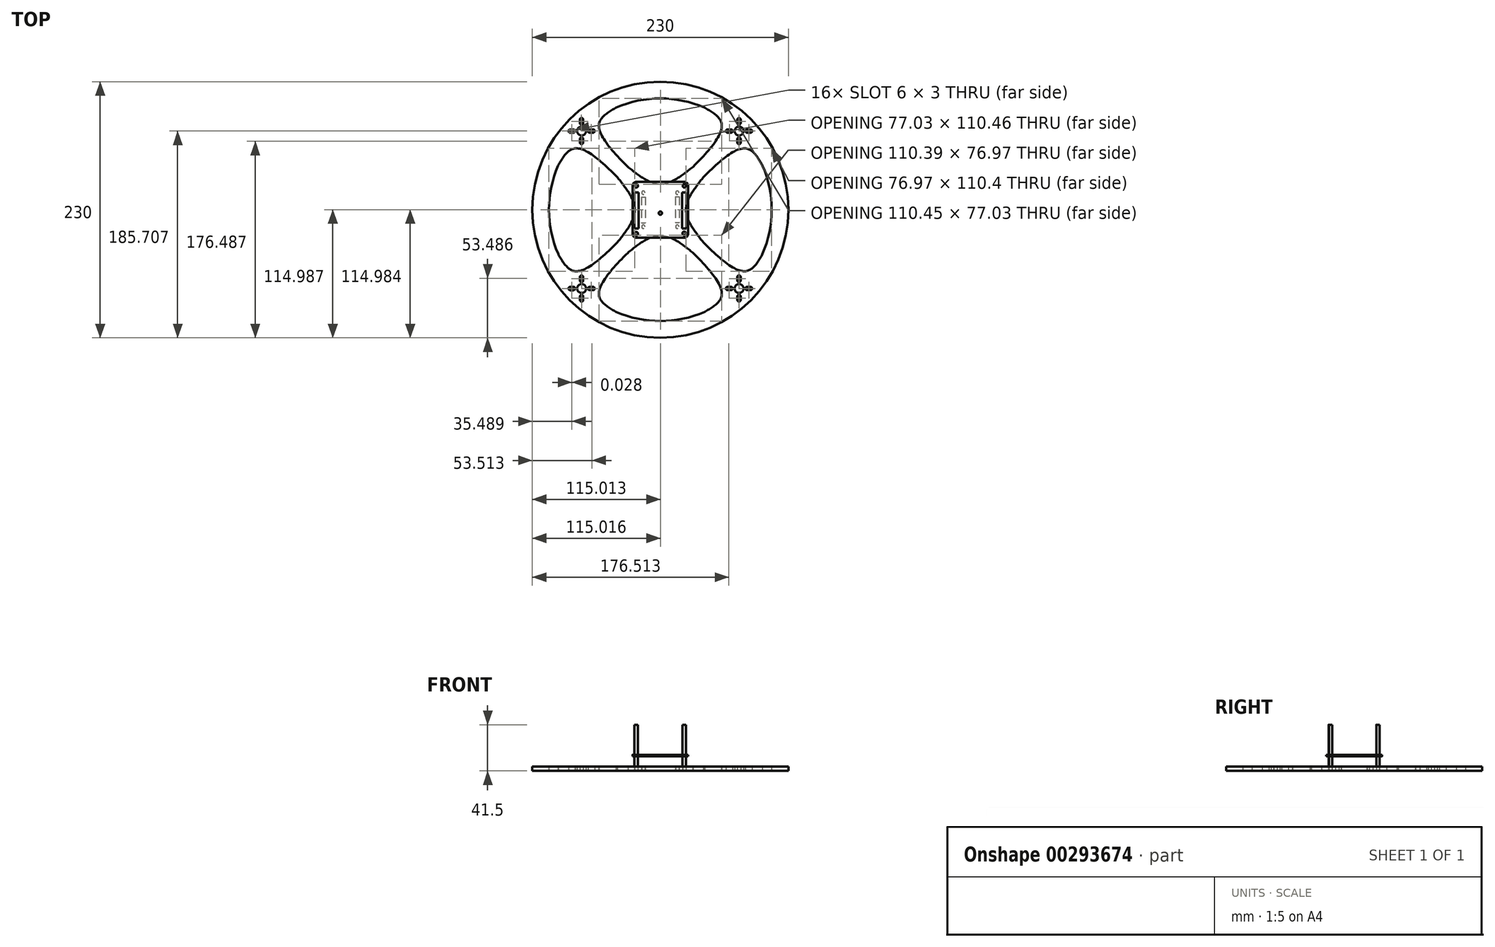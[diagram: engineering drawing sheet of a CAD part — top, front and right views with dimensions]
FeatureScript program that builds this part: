
annotation { "Feature Type Name" : "Feature", "Feature Type Description" : "" }
export const myFeature = defineFeature(function(context is Context, id is Id, definition is map)
    precondition{}
    {
        {
            var Q0;
            Q0=qCreatedBy(makeId("Top.planeOp"),FACE);
            var sketch = newSketch(context, id + "F0", { "sketchPlane" : qUnion([Q0])});
            skCircle(sketch, "E0", {"center": v(0, 0) * mm, "radius": 115 * mm});
            skCircle(sketch, "E1", {"center": v(0, 0) * mm, "radius": 100 * mm});
            skLineSegment(sketch, "E2.bottom", {"start": v(-17.97, 17.97) * mm, "end": v(18.03, 17.97) * mm});
            skLineSegment(sketch, "E2.left", {"start": v(-17.97, 17.97) * mm, "end": v(-17.97, -18.03) * mm});
            skLineSegment(sketch, "E2.right", {"start": v(18.03, 17.97) * mm, "end": v(18.03, -18.03) * mm});
            skLineSegment(sketch, "E3", {"start": v(-17.97, 17.97) * mm, "end": v(18.03, -18.03) * mm});
            skLineSegment(sketch, "E4", {"start": v(18.03, 17.97) * mm, "end": v(-17.97, -18.03) * mm});
            skLineSegment(sketch, "E5.bottom", {"start": v(-15.28, 15.28) * mm, "end": v(15.22, 15.28) * mm});
            skLineSegment(sketch, "E5.top", {"start": v(-15.28, -15.22) * mm, "end": v(15.22, -15.22) * mm});
            skLineSegment(sketch, "E5.left", {"start": v(-15.28, 15.28) * mm, "end": v(-15.28, -15.22) * mm});
            skLineSegment(sketch, "E5.right", {"start": v(15.22, 15.28) * mm, "end": v(15.22, -15.22) * mm});
            skCircle(sketch, "E6", {"center": v(-15.28, -15.22) * mm, "radius": 1.5 * mm});
            skCircle(sketch, "E7", {"center": v(15.22, -15.22) * mm, "radius": 1.5 * mm});
            skCircle(sketch, "E8", {"center": v(15.22, 15.28) * mm, "radius": 1.5 * mm});
            skCircle(sketch, "E9", {"center": v(-15.28, 15.28) * mm, "radius": 1.5 * mm});
            skLineSegment(sketch, "E10", {"start": v(18.03, 17.97) * mm, "end": v(-81.29, -81.35) * mm});
            skLineSegment(sketch, "E11", {"start": v(-81.29, -81.35) * mm, "end": v(81.34, 81.3) * mm});
            skLineSegment(sketch, "E12", {"start": v(-17.97, 17.97) * mm, "end": v(81.32, -81.32) * mm});
            skLineSegment(sketch, "E13", {"start": v(81.32, -81.32) * mm, "end": v(-81.32, 81.32) * mm});
            skPoint(sketch, "E14", {"position": v(-70.68, -70.74) * mm});
            skPoint(sketch, "E15", {"position": v(70.71, -70.71) * mm});
            skPoint(sketch, "E16", {"position": v(76.01, -76.01) * mm});
            skPoint(sketch, "E17", {"position": v(-63.56, -63.68) * mm});
            skPoint(sketch, "E18", {"position": v(-75.98, -76.04) * mm});
            skPoint(sketch, "E19", {"position": v(-65.18, -75.84) * mm});
            skPoint(sketch, "E20", {"position": v(-75.78, -65.24) * mm});
            skLineSegment(sketch, "E21", {"start": v(-65.18, -75.84) * mm, "end": v(-55.18, -75.84) * mm});
            skLineSegment(sketch, "E22", {"start": v(-75.78, -65.24) * mm, "end": v(-75.78, -55.24) * mm});
            skLineSegment(sketch, "E23", {"start": v(-17.97, -18.03) * mm, "end": v(18.03, -18.03) * mm});
            skPoint(sketch, "E24", {"position": v(65.21, -75.81) * mm});
            skPoint(sketch, "E25", {"position": v(75.81, -65.21) * mm});
            skPoint(sketch, "E26", {"position": v(65.24, 75.79) * mm});
            skPoint(sketch, "E27", {"position": v(75.83, 65.19) * mm});
            skPoint(sketch, "E28", {"position": v(-65.21, 75.81) * mm});
            skPoint(sketch, "E29", {"position": v(-75.81, 65.21) * mm});
            skPoint(sketch, "E30", {"position": v(70.73, 70.69) * mm});
            skPoint(sketch, "E31", {"position": v(-70.71, 70.71) * mm});
            skLineSegment(sketch, "E32", {"start": v(65.21, -75.81) * mm, "end": v(55.21, -75.81) * mm});
            skLineSegment(sketch, "E33", {"start": v(75.81, -65.21) * mm, "end": v(75.81, -55.21) * mm});
            skPoint(sketch, "E34", {"position": v(39.8, -91.74) * mm});
            skPoint(sketch, "E35", {"position": v(91.74, -39.8) * mm});
            skPoint(sketch, "E36", {"position": v(-39.75, -91.76) * mm});
            skPoint(sketch, "E37", {"position": v(-91.73, -39.83) * mm});
            skLineSegment(sketch, "E38", {"start": v(75.83, 65.19) * mm, "end": v(75.83, 55.19) * mm});
            skLineSegment(sketch, "E39", {"start": v(65.24, 75.79) * mm, "end": v(55.24, 75.79) * mm});
            skLineSegment(sketch, "E40", {"start": v(-65.21, 75.81) * mm, "end": v(-55.21, 75.81) * mm});
            skLineSegment(sketch, "E41", {"start": v(-75.81, 65.21) * mm, "end": v(-75.81, 55.21) * mm});
            skPoint(sketch, "E42", {"position": v(91.76, 39.76) * mm});
            skPoint(sketch, "E43", {"position": v(39.82, 91.73) * mm});
            skPoint(sketch, "E44", {"position": v(-39.8, 91.74) * mm});
            skPoint(sketch, "E45", {"position": v(-91.74, 39.8) * mm});
            skFitSpline(sketch, "E46", {"points": [v(-7.37, -18.03) * mm, v(-55.18, -75.84) * mm, v(-39.75, -91.76) * mm], "startDerivative": vector(-111.89, -103.5) * mm, "endDerivative": vector(64.51, -37.45) * mm});
            skFitSpline(sketch, "E47", {"points": [v(-17.97, -7.43) * mm, v(-75.78, -55.24) * mm, v(-91.73, -39.83) * mm], "startDerivative": vector(-103.48, -111.9) * mm, "endDerivative": vector(-37.52, 64.47) * mm});
            skFitSpline(sketch, "E48", {"points": [v(-17.97, 7.37) * mm, v(-75.81, 55.21) * mm, v(-91.74, 39.8) * mm], "startDerivative": vector(-103.54, 111.94) * mm, "endDerivative": vector(-37.49, -64.5) * mm});
            skFitSpline(sketch, "E49", {"points": [v(-7.37, 17.97) * mm, v(-55.21, 75.81) * mm, v(-39.8, 91.74) * mm], "startDerivative": vector(-111.94, 103.54) * mm, "endDerivative": vector(64.5, 37.49) * mm});
            skFitSpline(sketch, "E50", {"points": [v(7.43, 17.97) * mm, v(55.24, 75.79) * mm, v(39.82, 91.73) * mm], "startDerivative": vector(111.89, 103.5) * mm, "endDerivative": vector(-64.47, 37.51) * mm});
            skFitSpline(sketch, "E51", {"points": [v(18.03, 7.37) * mm, v(75.83, 55.19) * mm, v(91.76, 39.76) * mm], "startDerivative": vector(103.5, 111.9) * mm, "endDerivative": vector(37.46, -64.51) * mm});
            skFitSpline(sketch, "E52", {"points": [v(18.03, -7.43) * mm, v(75.81, -55.21) * mm, v(91.74, -39.8) * mm], "startDerivative": vector(103.45, -111.84) * mm, "endDerivative": vector(37.48, 64.48) * mm});
            skFitSpline(sketch, "E53", {"points": [v(7.43, -18.03) * mm, v(55.21, -75.81) * mm, v(39.8, -91.74) * mm], "startDerivative": vector(111.84, -103.45) * mm, "endDerivative": vector(-64.48, -37.48) * mm});
            skPoint(sketch, "E54", {"position": v(38.62, 29.2) * mm});
            skPoint(sketch, "E55", {"position": v(38.62, -29.24) * mm});
            skPoint(sketch, "E56", {"position": v(-38.56, -29.25) * mm});
            skPoint(sketch, "E57", {"position": v(-29.2, -38.62) * mm});
            skPoint(sketch, "E58", {"position": v(-38.56, 29.2) * mm});
            skPoint(sketch, "E59", {"position": v(-29.2, 38.56) * mm});
            skPoint(sketch, "E60", {"position": v(29.24, 38.57) * mm});
            skPoint(sketch, "E61", {"position": v(29.03, -38.4) * mm});
            skPoint(sketch, "E62", {"position": v(-22.97, -0.03) * mm});
            skPoint(sketch, "E62.positionSnap0", {"position": v(-17.97, -0.03) * mm});
            skFitSpline(sketch, "E63", {"points": [v(-38.56, 29.2) * mm, v(-22.97, -0.03) * mm, v(-38.56, -29.25) * mm], "startDerivative": vector(46.77, -58.44) * mm, "endDerivative": vector(-46.77, -58.44) * mm});
            skPoint(sketch, "E64", {"position": v(0, -23.03) * mm});
            skPoint(sketch, "E65", {"position": v(23.03, 0) * mm});
            skPoint(sketch, "E66", {"position": v(0, 22.97) * mm});
            skPoint(sketch, "E67", {"position": v(0, 17.97) * mm});
            skPoint(sketch, "E68", {"position": v(0, -18.03) * mm});
            skFitSpline(sketch, "E69", {"points": [v(-29.2, -38.62) * mm, v(0, -23.03) * mm, v(29.03, -38.4) * mm], "startDerivative": vector(58.3, 46.64) * mm, "endDerivative": vector(58.13, -46.26) * mm});
            skFitSpline(sketch, "E70", {"points": [v(38.62, -29.24) * mm, v(23.03, 0) * mm, v(38.62, 29.2) * mm], "startDerivative": vector(-46.77, 58.48) * mm, "endDerivative": vector(46.78, 58.4) * mm});
            skFitSpline(sketch, "E71", {"points": [v(-29.2, 38.56) * mm, v(0, 22.97) * mm, v(29.24, 38.57) * mm], "startDerivative": vector(58.4, -46.78) * mm, "endDerivative": vector(58.48, 46.77) * mm});
            skPoint(sketch, "E72", {"position": v(-70.7, 70.7) * mm});
            skCircle(sketch, "E73", {"center": v(-70.7, 70.7) * mm, "radius": 4 * mm});
            skLineSegment(sketch, "E74.left", {"start": v(-69.26, 63.46) * mm, "end": v(-69.26, 60.46) * mm});
            skLineSegment(sketch, "E75", {"start": v(-72.26, 63.46) * mm, "end": v(-72.26, 60.46) * mm});
            skArc(sketch, "E76", {"start": v(-69.26, 63.46) * mm, "mid": v(-70.76, 64.96) * mm, "end": v(-72.26, 63.46) * mm});
            skArc(sketch, "E77", {"start": v(-72.26, 60.46) * mm, "mid": v(-70.76, 58.96) * mm, "end": v(-69.26, 60.46) * mm});
            skLineSegment(sketch, "E78.left", {"start": v(-60.51, 69.21) * mm, "end": v(-63.51, 69.21) * mm});
            skLineSegment(sketch, "E79", {"start": v(-60.51, 72.21) * mm, "end": v(-63.51, 72.21) * mm});
            skArc(sketch, "E80", {"start": v(-60.51, 69.21) * mm, "mid": v(-59.01, 70.71) * mm, "end": v(-60.51, 72.21) * mm});
            skArc(sketch, "E81", {"start": v(-63.51, 72.21) * mm, "mid": v(-65.01, 70.71) * mm, "end": v(-63.51, 69.21) * mm});
            skLineSegment(sketch, "E82.left", {"start": v(-81.01, 72.2) * mm, "end": v(-78.01, 72.2) * mm});
            skLineSegment(sketch, "E83", {"start": v(-81.01, 69.2) * mm, "end": v(-78.01, 69.2) * mm});
            skArc(sketch, "E84", {"start": v(-81.01, 72.2) * mm, "mid": v(-82.51, 70.7) * mm, "end": v(-81.01, 69.2) * mm});
            skArc(sketch, "E85", {"start": v(-78.01, 69.2) * mm, "mid": v(-76.51, 70.7) * mm, "end": v(-78.01, 72.2) * mm});
            skLineSegment(sketch, "E86.left", {"start": v(-69.3, 80.96) * mm, "end": v(-69.3, 77.96) * mm});
            skLineSegment(sketch, "E87", {"start": v(-72.3, 80.96) * mm, "end": v(-72.3, 77.96) * mm});
            skArc(sketch, "E88", {"start": v(-69.3, 80.96) * mm, "mid": v(-70.8, 82.46) * mm, "end": v(-72.3, 80.96) * mm});
            skArc(sketch, "E89", {"start": v(-72.3, 77.96) * mm, "mid": v(-70.8, 76.46) * mm, "end": v(-69.3, 77.96) * mm});
            skCircle(sketch, "E90", {"center": v(-70.68, -70.74) * mm, "radius": 4 * mm});
            skLineSegment(sketch, "E91.left", {"start": v(-69.23, -78) * mm, "end": v(-69.23, -81) * mm});
            skLineSegment(sketch, "E92", {"start": v(-72.23, -78) * mm, "end": v(-72.23, -81) * mm});
            skArc(sketch, "E93", {"start": v(-69.23, -78) * mm, "mid": v(-70.73, -76.5) * mm, "end": v(-72.23, -78) * mm});
            skArc(sketch, "E94", {"start": v(-72.23, -81) * mm, "mid": v(-70.73, -82.5) * mm, "end": v(-69.23, -81) * mm});
            skLineSegment(sketch, "E95.left", {"start": v(-60.48, -72.24) * mm, "end": v(-63.48, -72.24) * mm});
            skLineSegment(sketch, "E96", {"start": v(-60.48, -69.24) * mm, "end": v(-63.48, -69.24) * mm});
            skArc(sketch, "E97", {"start": v(-60.48, -72.24) * mm, "mid": v(-58.98, -70.74) * mm, "end": v(-60.48, -69.24) * mm});
            skArc(sketch, "E98", {"start": v(-63.48, -69.24) * mm, "mid": v(-64.98, -70.74) * mm, "end": v(-63.48, -72.24) * mm});
            skLineSegment(sketch, "E99.left", {"start": v(-80.98, -69.24) * mm, "end": v(-77.98, -69.24) * mm});
            skLineSegment(sketch, "E100", {"start": v(-80.98, -72.24) * mm, "end": v(-77.98, -72.24) * mm});
            skArc(sketch, "E101", {"start": v(-80.98, -69.24) * mm, "mid": v(-82.48, -70.74) * mm, "end": v(-80.98, -72.24) * mm});
            skArc(sketch, "E102", {"start": v(-77.98, -72.24) * mm, "mid": v(-76.48, -70.74) * mm, "end": v(-77.98, -69.24) * mm});
            skLineSegment(sketch, "E103.left", {"start": v(-69.27, -60.5) * mm, "end": v(-69.27, -63.5) * mm});
            skLineSegment(sketch, "E104", {"start": v(-72.27, -60.5) * mm, "end": v(-72.27, -63.5) * mm});
            skArc(sketch, "E105", {"start": v(-69.27, -60.5) * mm, "mid": v(-70.77, -59) * mm, "end": v(-72.27, -60.5) * mm});
            skArc(sketch, "E106", {"start": v(-72.27, -63.5) * mm, "mid": v(-70.77, -65) * mm, "end": v(-69.27, -63.5) * mm});
            skCircle(sketch, "E107", {"center": v(70.71, -70.71) * mm, "radius": 4 * mm});
            skLineSegment(sketch, "E108.left", {"start": v(72.16, -77.96) * mm, "end": v(72.16, -80.96) * mm});
            skLineSegment(sketch, "E109", {"start": v(69.16, -77.96) * mm, "end": v(69.16, -80.96) * mm});
            skArc(sketch, "E110", {"start": v(72.16, -77.96) * mm, "mid": v(70.66, -76.46) * mm, "end": v(69.16, -77.96) * mm});
            skArc(sketch, "E111", {"start": v(69.16, -80.96) * mm, "mid": v(70.66, -82.46) * mm, "end": v(72.16, -80.96) * mm});
            skLineSegment(sketch, "E112.left", {"start": v(80.9, -72.2) * mm, "end": v(77.9, -72.2) * mm});
            skLineSegment(sketch, "E113", {"start": v(80.9, -69.2) * mm, "end": v(77.9, -69.2) * mm});
            skArc(sketch, "E114", {"start": v(80.9, -72.2) * mm, "mid": v(82.4, -70.7) * mm, "end": v(80.9, -69.2) * mm});
            skArc(sketch, "E115", {"start": v(77.9, -69.2) * mm, "mid": v(76.4, -70.7) * mm, "end": v(77.9, -72.2) * mm});
            skLineSegment(sketch, "E116.left", {"start": v(60.4, -69.21) * mm, "end": v(63.4, -69.21) * mm});
            skLineSegment(sketch, "E117", {"start": v(60.4, -72.21) * mm, "end": v(63.4, -72.21) * mm});
            skArc(sketch, "E118", {"start": v(60.4, -69.21) * mm, "mid": v(58.9, -70.71) * mm, "end": v(60.4, -72.21) * mm});
            skArc(sketch, "E119", {"start": v(63.4, -72.21) * mm, "mid": v(64.9, -70.71) * mm, "end": v(63.4, -69.21) * mm});
            skLineSegment(sketch, "E120.left", {"start": v(72.13, -60.46) * mm, "end": v(72.13, -63.46) * mm});
            skLineSegment(sketch, "E121", {"start": v(69.13, -60.46) * mm, "end": v(69.13, -63.46) * mm});
            skArc(sketch, "E122", {"start": v(72.13, -60.46) * mm, "mid": v(70.63, -58.96) * mm, "end": v(69.13, -60.46) * mm});
            skArc(sketch, "E123", {"start": v(69.13, -63.46) * mm, "mid": v(70.63, -64.96) * mm, "end": v(72.13, -63.46) * mm});
            skCircle(sketch, "E124", {"center": v(70.73, 70.69) * mm, "radius": 4 * mm});
            skLineSegment(sketch, "E125.left", {"start": v(72.18, 63.44) * mm, "end": v(72.18, 60.44) * mm});
            skLineSegment(sketch, "E126", {"start": v(69.18, 63.44) * mm, "end": v(69.18, 60.44) * mm});
            skArc(sketch, "E127", {"start": v(72.18, 63.44) * mm, "mid": v(70.68, 64.94) * mm, "end": v(69.18, 63.44) * mm});
            skArc(sketch, "E128", {"start": v(69.18, 60.44) * mm, "mid": v(70.68, 58.94) * mm, "end": v(72.18, 60.44) * mm});
            skLineSegment(sketch, "E129.left", {"start": v(80.93, 69.19) * mm, "end": v(77.93, 69.19) * mm});
            skLineSegment(sketch, "E130", {"start": v(80.93, 72.19) * mm, "end": v(77.93, 72.19) * mm});
            skArc(sketch, "E131", {"start": v(80.93, 69.19) * mm, "mid": v(82.43, 70.69) * mm, "end": v(80.93, 72.19) * mm});
            skArc(sketch, "E132", {"start": v(77.93, 72.19) * mm, "mid": v(76.43, 70.69) * mm, "end": v(77.93, 69.19) * mm});
            skLineSegment(sketch, "E133.left", {"start": v(60.43, 72.18) * mm, "end": v(63.43, 72.18) * mm});
            skLineSegment(sketch, "E134", {"start": v(60.43, 69.18) * mm, "end": v(63.43, 69.18) * mm});
            skArc(sketch, "E135", {"start": v(60.43, 72.18) * mm, "mid": v(58.93, 70.68) * mm, "end": v(60.43, 69.18) * mm});
            skArc(sketch, "E136", {"start": v(63.43, 69.18) * mm, "mid": v(64.93, 70.68) * mm, "end": v(63.43, 72.18) * mm});
            skLineSegment(sketch, "E137.left", {"start": v(72.15, 80.94) * mm, "end": v(72.15, 77.94) * mm});
            skLineSegment(sketch, "E138", {"start": v(69.15, 80.94) * mm, "end": v(69.15, 77.94) * mm});
            skArc(sketch, "E139", {"start": v(72.15, 80.94) * mm, "mid": v(70.65, 82.44) * mm, "end": v(69.15, 80.94) * mm});
            skArc(sketch, "E140", {"start": v(69.15, 77.94) * mm, "mid": v(70.65, 76.44) * mm, "end": v(72.15, 77.94) * mm});
            skPoint(sketch, "E141", {"position": v(-21.5, -21.56) * mm});
            skCircle(sketch, "E142", {"center": v(-21.5, -21.56) * mm, "radius": 1.5 * mm});
            skPoint(sketch, "E143", {"position": v(21.56, -21.56) * mm});
            skPoint(sketch, "E144", {"position": v(21.56, 21.5) * mm});
            skPoint(sketch, "E145", {"position": v(-21.5, 21.5) * mm});
            skCircle(sketch, "E146", {"center": v(-21.5, 21.5) * mm, "radius": 1.5 * mm});
            skCircle(sketch, "E147", {"center": v(21.56, 21.5) * mm, "radius": 1.5 * mm});
            skCircle(sketch, "E148", {"center": v(21.56, -21.56) * mm, "radius": 1.5 * mm});
            skLineSegment(sketch, "E149.left", {"start": v(-15.24, 11.66) * mm, "end": v(-15.24, -11.59) * mm});
            skLineSegment(sketch, "E150.left", {"start": v(15.22, 11.64) * mm, "end": v(15.22, -11.61) * mm});
            skLineSegment(sketch, "E151.bottom", {"start": v(-17.03, 11.57) * mm, "end": v(-13.53, 11.57) * mm});
            skLineSegment(sketch, "E151.top", {"start": v(-17.03, -11.68) * mm, "end": v(-13.53, -11.68) * mm});
            skLineSegment(sketch, "E151.left", {"start": v(-17.03, 11.57) * mm, "end": v(-17.03, -11.68) * mm});
            skLineSegment(sketch, "E151.right", {"start": v(-13.53, 11.57) * mm, "end": v(-13.53, -11.68) * mm});
            skLineSegment(sketch, "E152.bottom", {"start": v(13.37, 11.76) * mm, "end": v(16.87, 11.76) * mm});
            skLineSegment(sketch, "E152.top", {"start": v(13.37, -11.5) * mm, "end": v(16.87, -11.5) * mm});
            skLineSegment(sketch, "E152.left", {"start": v(13.37, 11.76) * mm, "end": v(13.37, -11.5) * mm});
            skLineSegment(sketch, "E152.right", {"start": v(16.87, 11.76) * mm, "end": v(16.87, -11.5) * mm});
            skSolve(sketch);
        }
        {
            var Q0;
            Q0=qCreatedBy(makeId("Top.planeOp"),FACE);
            var sketch = newSketch(context, id + "F1", { "sketchPlane" : qUnion([Q0])});
            skLineSegment(sketch, "E153.bottom", {"start": v(21.53, 21.51) * mm, "end": v(-21.54, 21.51) * mm});
            skLineSegment(sketch, "E153.top", {"start": v(21.53, -21.56) * mm, "end": v(-21.54, -21.56) * mm});
            skLineSegment(sketch, "E153.left", {"start": v(21.53, 21.51) * mm, "end": v(21.53, -21.56) * mm});
            skLineSegment(sketch, "E153.right", {"start": v(-21.54, 21.51) * mm, "end": v(-21.54, -21.56) * mm});
            skPoint(sketch, "E153.middle", {"position": v(0, -0.02) * mm});
            skCircle(sketch, "E154", {"center": v(-21.54, -21.56) * mm, "radius": 1.5 * mm});
            skCircle(sketch, "E155", {"center": v(21.53, -21.56) * mm, "radius": 1.5 * mm});
            skCircle(sketch, "E156", {"center": v(21.53, 21.51) * mm, "radius": 1.5 * mm});
            skCircle(sketch, "E157", {"center": v(-21.54, 21.51) * mm, "radius": 1.5 * mm});
            skLineSegment(sketch, "E158.bottom", {"start": v(-25, 24.98) * mm, "end": v(25, 24.98) * mm});
            skLineSegment(sketch, "E158.top", {"start": v(-25, -25.02) * mm, "end": v(25, -25.02) * mm});
            skLineSegment(sketch, "E158.left", {"start": v(-25, 24.98) * mm, "end": v(-25, -25.02) * mm});
            skLineSegment(sketch, "E158.right", {"start": v(25, 24.98) * mm, "end": v(25, -25.02) * mm});
            skArc(sketch, "E159", {"start": v(21.53, -25.02) * mm, "mid": v(23.98, -24) * mm, "end": v(25, -21.56) * mm});
            skArc(sketch, "E160", {"start": v(-21.54, -25.02) * mm, "mid": v(-24, -24) * mm, "end": v(-25, -21.56) * mm});
            skArc(sketch, "E161", {"start": v(-25, 21.51) * mm, "mid": v(-24, 23.96) * mm, "end": v(-21.54, 24.98) * mm});
            skArc(sketch, "E162", {"start": v(25, 21.51) * mm, "mid": v(23.98, 23.96) * mm, "end": v(21.53, 24.98) * mm});
            skPoint(sketch, "E163", {"position": v(0, -3.02) * mm});
            skCircle(sketch, "E164", {"center": v(0, -3.02) * mm, "radius": 1.5 * mm});
            skLineSegment(sketch, "E165.bottom", {"start": v(-23.36, 15.7) * mm, "end": v(-19.58, 15.7) * mm});
            skLineSegment(sketch, "E165.top", {"start": v(-23.36, -16.77) * mm, "end": v(-19.58, -16.77) * mm});
            skLineSegment(sketch, "E165.left", {"start": v(-23.36, 15.7) * mm, "end": v(-23.36, -16.77) * mm});
            skLineSegment(sketch, "E165.right", {"start": v(-19.58, 15.7) * mm, "end": v(-19.58, -16.77) * mm});
            skLineSegment(sketch, "E166.bottom", {"start": v(19.67, 15.7) * mm, "end": v(23.45, 15.7) * mm});
            skLineSegment(sketch, "E166.top", {"start": v(19.67, -16.77) * mm, "end": v(23.45, -16.77) * mm});
            skLineSegment(sketch, "E166.left", {"start": v(19.67, 15.7) * mm, "end": v(19.67, -16.77) * mm});
            skLineSegment(sketch, "E166.right", {"start": v(23.45, 15.7) * mm, "end": v(23.45, -16.77) * mm});
            skSolve(sketch);
        }
        {
            var Q0;
            {var subQ8=sQuery(id+"F1.wireOp",EDGE,"E159");Q0=makeQuery(id+"F1.imprint","IMPRINT",FACE,{"disambiguationData":[TD([[makeQuery(id+"F1.imprint","IMPRINT",EDGE,{"derivedFrom":subQ8}),1.0]])]});}
            var Q1;
            Q1=makeQuery(id+"F1.imprint","IMPRINT",FACE,{"disambiguationData":[TD([[makeQuery(id+"F1.imprint","IMPRINT",EDGE,{"derivedFrom":sQuery(id+"F1.wireOp",EDGE,"E164")}),-1.0]])]});
            extrude(context, id + "F2", {"entities" : qUnion([Q0, Q1]), "depth" : 1.5 * mm});
        }
        {
            var Q0;
            Q0=makeQuery(id+"F2.opExtrude","SWEPT_BODY",BODY,{"disambiguationData":[OSD([sQuery(id+"F1.wireOp",EDGE,"E154"),sQuery(id+"F1.wireOp",EDGE,"E155"),sQuery(id+"F1.wireOp",EDGE,"E156"),sQuery(id+"F1.wireOp",EDGE,"E157"),sQuery(id+"F1.wireOp",EDGE,"E158.bottom"),sQuery(id+"F1.wireOp",EDGE,"E158.top"),sQuery(id+"F1.wireOp",EDGE,"E158.left"),sQuery(id+"F1.wireOp",EDGE,"E158.right"),sQuery(id+"F1.wireOp",EDGE,"E159"),sQuery(id+"F1.wireOp",EDGE,"E160"),sQuery(id+"F1.wireOp",EDGE,"E161"),sQuery(id+"F1.wireOp",EDGE,"E162"),sQuery(id+"F1.wireOp",EDGE,"E164"),sQuery(id+"F1.wireOp",EDGE,"E165.bottom"),sQuery(id+"F1.wireOp",EDGE,"E165.top"),sQuery(id+"F1.wireOp",EDGE,"E165.left"),sQuery(id+"F1.wireOp",EDGE,"E165.right"),sQuery(id+"F1.wireOp",EDGE,"E166.bottom"),sQuery(id+"F1.wireOp",EDGE,"E166.top"),sQuery(id+"F1.wireOp",EDGE,"E166.left"),sQuery(id+"F1.wireOp",EDGE,"E166.right")])]});
            transform(context, id + "F3", {"entities" : qUnion([Q0]), "transformType" : TransformType.TRANSLATION_3D, "dx" : 0 * mm, "dy" : 0 * mm, "dz" : 13 * mm, "makeCopy" : false});
        }
        {
            var Q0;
            Q0=qCreatedBy(makeId("Top.planeOp"),FACE);
            var sketch = newSketch(context, id + "F4", { "sketchPlane" : qUnion([Q0])});
            skCircle(sketch, "E167", {"center": v(-21.74, 21.47) * mm, "radius": 1.5 * mm});
            skCircle(sketch, "E168", {"center": v(21.56, 21.47) * mm, "radius": 1.5 * mm});
            skCircle(sketch, "E169", {"center": v(21.42, -21.1) * mm, "radius": 1.5 * mm});
            skCircle(sketch, "E170", {"center": v(-21.74, -21.4) * mm, "radius": 1.5 * mm});
            skSolve(sketch);
        }
        {
            var Q0;
            Q0=makeQuery(id+"F4.imprint","IMPRINT",FACE,{"disambiguationData":[TD([[makeQuery(id+"F4.imprint","IMPRINT",EDGE,{"derivedFrom":sQuery(id+"F4.wireOp",EDGE,"E167")}),1.0]])]});
            var Q1;
            Q1=makeQuery(id+"F4.imprint","IMPRINT",FACE,{"disambiguationData":[TD([[makeQuery(id+"F4.imprint","IMPRINT",EDGE,{"derivedFrom":sQuery(id+"F4.wireOp",EDGE,"E170")}),1.0]])]});
            var Q2;
            Q2=makeQuery(id+"F4.imprint","IMPRINT",FACE,{"disambiguationData":[TD([[makeQuery(id+"F4.imprint","IMPRINT",EDGE,{"derivedFrom":sQuery(id+"F4.wireOp",EDGE,"E169")}),1.0]])]});
            var Q3;
            Q3=makeQuery(id+"F4.imprint","IMPRINT",FACE,{"disambiguationData":[TD([[makeQuery(id+"F4.imprint","IMPRINT",EDGE,{"derivedFrom":sQuery(id+"F4.wireOp",EDGE,"E168")}),1.0]])]});
            extrude(context, id + "F5", {"entities" : qUnion([Q0, Q1, Q2, Q3]), "depth" : 41.5 * mm});
        }
        {
            var Q0;
            Q0=makeQuery(id+"F0.imprint","IMPRINT",FACE,{"disambiguationData":[TD([[makeQuery(id+"F0.imprint","IMPRINT",EDGE,{"derivedFrom":sQuery(id+"F0.wireOp",EDGE,"E82.left")}),1.0]])]});
            var Q1;
            Q1=makeQuery(id+"F0.imprint","IMPRINT",FACE,{"disambiguationData":[TD([[makeQuery(id+"F0.imprint","IMPRINT",EDGE,{"derivedFrom":sQuery(id+"F0.wireOp",EDGE,"E91.left")}),1.0]])]});
            var Q2;
            {var subQ1=sQuery(id+"F0.wireOp",EDGE,"E21");Q2=makeQuery(id+"F0.imprint","IMPRINT",FACE,{"disambiguationData":[TD([[makeQuery(id+"F0.imprint","IMPRINT",EDGE,{"derivedFrom":subQ1}),1.0]])]});}
            var Q3;
            {var subQ6=sQuery(id+"F0.wireOp",EDGE,"E22");Q3=makeQuery(id+"F0.imprint","IMPRINT",FACE,{"disambiguationData":[TD([[makeQuery(id+"F0.imprint","IMPRINT",EDGE,{"derivedFrom":subQ6}),-1.0]])]});}
            var Q4;
            {var subQ0=sQuery(id+"F0.wireOp",EDGE,"E22");Q4=makeQuery(id+"F0.imprint","IMPRINT",FACE,{"disambiguationData":[TD([[makeQuery(id+"F0.imprint","IMPRINT",EDGE,{"derivedFrom":subQ0}),1.0]])]});}
            var Q5;
            {var subQ0=sQuery(id+"F0.wireOp",EDGE,"E21");Q5=makeQuery(id+"F0.imprint","IMPRINT",FACE,{"disambiguationData":[TD([[makeQuery(id+"F0.imprint","IMPRINT",EDGE,{"derivedFrom":subQ0}),-1.0]])]});}
            var Q6;
            {var subQ0=sQuery(id+"F0.wireOp",EDGE,"E32");Q6=makeQuery(id+"F0.imprint","IMPRINT",FACE,{"disambiguationData":[TD([[makeQuery(id+"F0.imprint","IMPRINT",EDGE,{"derivedFrom":subQ0}),1.0]])]});}
            var Q7;
            {var subQ1=sQuery(id+"F0.wireOp",EDGE,"E32");Q7=makeQuery(id+"F0.imprint","IMPRINT",FACE,{"disambiguationData":[TD([[makeQuery(id+"F0.imprint","IMPRINT",EDGE,{"derivedFrom":subQ1}),-1.0]])]});}
            var Q8;
            {var subQ5=sQuery(id+"F0.wireOp",EDGE,"E33");Q8=makeQuery(id+"F0.imprint","IMPRINT",FACE,{"disambiguationData":[TD([[makeQuery(id+"F0.imprint","IMPRINT",EDGE,{"derivedFrom":subQ5}),1.0]])]});}
            var Q9;
            Q9=makeQuery(id+"F0.imprint","IMPRINT",FACE,{"disambiguationData":[TD([[makeQuery(id+"F0.imprint","IMPRINT",EDGE,{"derivedFrom":sQuery(id+"F0.wireOp",EDGE,"E112.left")}),1.0]])]});
            var Q10;
            {var subQ0=sQuery(id+"F0.wireOp",EDGE,"E33");Q10=makeQuery(id+"F0.imprint","IMPRINT",FACE,{"disambiguationData":[TD([[makeQuery(id+"F0.imprint","IMPRINT",EDGE,{"derivedFrom":subQ0}),-1.0]])]});}
            var Q11;
            {var subQ5=sQuery(id+"F0.wireOp",EDGE,"E70");Q11=makeQuery(id+"F0.imprint","IMPRINT",FACE,{"disambiguationData":[TD([[makeQuery(id+"F0.imprint","IMPRINT",EDGE,{"derivedFrom":subQ5}),1.0]])]});}
            var Q12;
            {var subQ5=sQuery(id+"F0.wireOp",EDGE,"E38");Q12=makeQuery(id+"F0.imprint","IMPRINT",FACE,{"disambiguationData":[TD([[makeQuery(id+"F0.imprint","IMPRINT",EDGE,{"derivedFrom":subQ5}),-1.0]])]});}
            var Q13;
            {var subQ6=sQuery(id+"F0.wireOp",EDGE,"E39");Q13=makeQuery(id+"F0.imprint","IMPRINT",FACE,{"disambiguationData":[TD([[makeQuery(id+"F0.imprint","IMPRINT",EDGE,{"derivedFrom":subQ6}),1.0]])]});}
            var Q14;
            {var subQ5=sQuery(id+"F0.wireOp",EDGE,"E71");Q14=makeQuery(id+"F0.imprint","IMPRINT",FACE,{"disambiguationData":[TD([[makeQuery(id+"F0.imprint","IMPRINT",EDGE,{"derivedFrom":subQ5}),-1.0]])]});}
            var Q15;
            {var subQ1=sQuery(id+"F0.wireOp",EDGE,"E2.bottom");var subQ9=makeQuery(id+"F0.imprint","INTERSECT",VERTEX,{"derivedFrom":[subQ1,sQuery(id+"F0.wireOp",EDGE,"E49")]});Q15=makeQuery(id+"F0.imprint","IMPRINT",FACE,{"disambiguationData":[TD([[makeQuery(id+"F0.imprint","IMPRINT",EDGE,{"disambiguationData":[TD([[subQ9,-1.0]])],"derivedFrom":subQ1}),-1.0]])]});}
            var Q16;
            {var subQ5=sQuery(id+"F0.wireOp",EDGE,"E9");var subQ6=sQuery(id+"F0.wireOp",EDGE,"E5.bottom");var subQ7=makeQuery(id+"F0.imprint","INTERSECT",VERTEX,{"derivedFrom":[subQ6,subQ5]});Q16=makeQuery(id+"F0.imprint","IMPRINT",FACE,{"disambiguationData":[TD([[makeQuery(id+"F0.imprint","IMPRINT",EDGE,{"disambiguationData":[TD([[subQ7,-1.0]])],"derivedFrom":subQ6}),-1.0]])]});}
            var Q17;
            {var subQ1=sQuery(id+"F0.wireOp",EDGE,"E6");var subQ6=sQuery(id+"F0.wireOp",EDGE,"E5.top");var subQ9=makeQuery(id+"F0.imprint","INTERSECT",VERTEX,{"derivedFrom":[subQ6,subQ1]});Q17=makeQuery(id+"F0.imprint","IMPRINT",FACE,{"disambiguationData":[TD([[makeQuery(id+"F0.imprint","IMPRINT",EDGE,{"disambiguationData":[TD([[subQ9,-1.0]])],"derivedFrom":subQ6}),1.0]])]});}
            var Q18;
            {var subQ1=sQuery(id+"F0.wireOp",EDGE,"E8");var subQ6=sQuery(id+"F0.wireOp",EDGE,"E5.right");var subQ9=makeQuery(id+"F0.imprint","INTERSECT",VERTEX,{"derivedFrom":[subQ6,subQ1]});Q18=makeQuery(id+"F0.imprint","IMPRINT",FACE,{"disambiguationData":[TD([[makeQuery(id+"F0.imprint","IMPRINT",EDGE,{"disambiguationData":[TD([[subQ9,-1.0]])],"derivedFrom":subQ6}),-1.0]])]});}
            var Q19;
            {var subQ3=sQuery(id+"F0.wireOp",EDGE,"E6");var subQ5=sQuery(id+"F0.wireOp",EDGE,"E5.top");var subQ6=makeQuery(id+"F0.imprint","INTERSECT",VERTEX,{"derivedFrom":[subQ5,subQ3]});Q19=makeQuery(id+"F0.imprint","IMPRINT",FACE,{"disambiguationData":[TD([[makeQuery(id+"F0.imprint","IMPRINT",EDGE,{"disambiguationData":[TD([[subQ6,-1.0]])],"derivedFrom":subQ5}),-1.0]])]});}
            var Q20;
            {var subQ6=sQuery(id+"F0.wireOp",EDGE,"E2.left");var subQ11=makeQuery(id+"F0.imprint","INTERSECT",VERTEX,{"derivedFrom":[subQ6,sQuery(id+"F0.wireOp",EDGE,"E47")]});Q20=makeQuery(id+"F0.imprint","IMPRINT",FACE,{"disambiguationData":[TD([[makeQuery(id+"F0.imprint","IMPRINT",EDGE,{"disambiguationData":[TD([[subQ11,1.0]])],"derivedFrom":subQ6}),1.0]])]});}
            var Q21;
            {var subQ5=sQuery(id+"F0.wireOp",EDGE,"E9");var subQ6=sQuery(id+"F0.wireOp",EDGE,"E5.left");var subQ7=makeQuery(id+"F0.imprint","INTERSECT",VERTEX,{"derivedFrom":[subQ6,subQ5]});Q21=makeQuery(id+"F0.imprint","IMPRINT",FACE,{"disambiguationData":[TD([[makeQuery(id+"F0.imprint","IMPRINT",EDGE,{"disambiguationData":[TD([[subQ7,-1.0]])],"derivedFrom":subQ6}),1.0]])]});}
            var Q22;
            {var subQ5=sQuery(id+"F0.wireOp",EDGE,"E69");Q22=makeQuery(id+"F0.imprint","IMPRINT",FACE,{"disambiguationData":[TD([[makeQuery(id+"F0.imprint","IMPRINT",EDGE,{"derivedFrom":subQ5}),1.0]])]});}
            var Q23;
            {var subQ1=sQuery(id+"F0.wireOp",EDGE,"E2.right");var subQ12=makeQuery(id+"F0.imprint","INTERSECT",VERTEX,{"derivedFrom":[subQ1,sQuery(id+"F0.wireOp",EDGE,"E51")]});Q23=makeQuery(id+"F0.imprint","IMPRINT",FACE,{"disambiguationData":[TD([[makeQuery(id+"F0.imprint","IMPRINT",EDGE,{"disambiguationData":[TD([[subQ12,-1.0]])],"derivedFrom":subQ1}),-1.0]])]});}
            var Q24;
            {var subQ5=sQuery(id+"F0.wireOp",EDGE,"E63");Q24=makeQuery(id+"F0.imprint","IMPRINT",FACE,{"disambiguationData":[TD([[makeQuery(id+"F0.imprint","IMPRINT",EDGE,{"derivedFrom":subQ5}),1.0]])]});}
            var Q25;
            {var subQ6=sQuery(id+"F0.wireOp",EDGE,"E41");Q25=makeQuery(id+"F0.imprint","IMPRINT",FACE,{"disambiguationData":[TD([[makeQuery(id+"F0.imprint","IMPRINT",EDGE,{"derivedFrom":subQ6}),1.0]])]});}
            var Q26;
            {var subQ1=sQuery(id+"F0.wireOp",EDGE,"E40");Q26=makeQuery(id+"F0.imprint","IMPRINT",FACE,{"disambiguationData":[TD([[makeQuery(id+"F0.imprint","IMPRINT",EDGE,{"derivedFrom":subQ1}),-1.0]])]});}
            var Q27;
            {var subQ0=sQuery(id+"F0.wireOp",EDGE,"E41");Q27=makeQuery(id+"F0.imprint","IMPRINT",FACE,{"disambiguationData":[TD([[makeQuery(id+"F0.imprint","IMPRINT",EDGE,{"derivedFrom":subQ0}),-1.0]])]});}
            var Q28;
            Q28=makeQuery(id+"F0.imprint","IMPRINT",FACE,{"disambiguationData":[TD([[makeQuery(id+"F0.imprint","IMPRINT",EDGE,{"derivedFrom":sQuery(id+"F0.wireOp",EDGE,"E86.left")}),1.0]])]});
            var Q29;
            {var subQ0=sQuery(id+"F0.wireOp",EDGE,"E40");Q29=makeQuery(id+"F0.imprint","IMPRINT",FACE,{"disambiguationData":[TD([[makeQuery(id+"F0.imprint","IMPRINT",EDGE,{"derivedFrom":subQ0}),1.0]])]});}
            var Q30;
            {var subQ0=sQuery(id+"F0.wireOp",EDGE,"E39");Q30=makeQuery(id+"F0.imprint","IMPRINT",FACE,{"disambiguationData":[TD([[makeQuery(id+"F0.imprint","IMPRINT",EDGE,{"derivedFrom":subQ0}),-1.0]])]});}
            var Q31;
            {var subQ0=sQuery(id+"F0.wireOp",EDGE,"E38");Q31=makeQuery(id+"F0.imprint","IMPRINT",FACE,{"disambiguationData":[TD([[makeQuery(id+"F0.imprint","IMPRINT",EDGE,{"derivedFrom":subQ0}),1.0]])]});}
            extrude(context, id + "F6", {"entities" : qUnion([Q0, Q1, Q2, Q3, Q4, Q5, Q6, Q7, Q8, Q9, Q10, Q11, Q12, Q13, Q14, Q15, Q16, Q17, Q18, Q19, Q20, Q21, Q22, Q23, Q24, Q25, Q26, Q27, Q28, Q29, Q30, Q31]), "depth" : 4 * mm});
        }
    });
